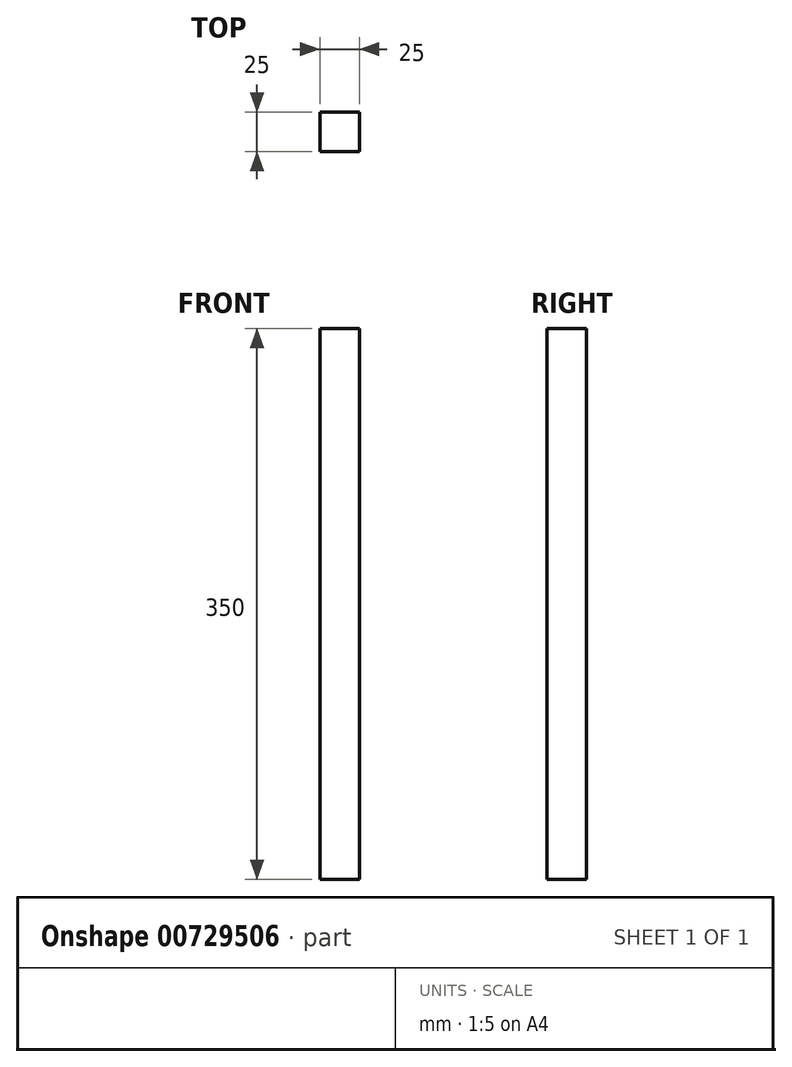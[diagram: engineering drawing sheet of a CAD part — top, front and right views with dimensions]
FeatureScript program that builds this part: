
annotation { "Feature Type Name" : "Feature", "Feature Type Description" : "" }
export const myFeature = defineFeature(function(context is Context, id is Id, definition is map)
    precondition{}
    {
        {
            var Q0;
            Q0=qCreatedBy(makeId("Top.planeOp"),FACE);
            var sketch = newSketch(context, id + "F0", { "sketchPlane" : qUnion([Q0])});
            skLineSegment(sketch, "E0.bottom", {"start": v(-2.89, -1.45) * mm, "end": v(22.11, -1.45) * mm});
            skLineSegment(sketch, "E0.top", {"start": v(-2.89, -26.45) * mm, "end": v(22.11, -26.45) * mm});
            skLineSegment(sketch, "E0.left", {"start": v(-2.89, -1.45) * mm, "end": v(-2.89, -26.45) * mm});
            skLineSegment(sketch, "E0.right", {"start": v(22.11, -1.45) * mm, "end": v(22.11, -26.45) * mm});
            skSolve(sketch);
        }
        {
            var Q0;
            Q0=makeQuery(id+"F0.imprint","IMPRINT",FACE,{"disambiguationData":[TD([[makeQuery(id+"F0.imprint","IMPRINT",EDGE,{"derivedFrom":sQuery(id+"F0.wireOp",EDGE,"E0.bottom")}),-1.0]])]});
            extrude(context, id + "F1", {"entities" : qUnion([Q0]), "oppositeDirection" : true, "depth" : 350 * mm, "offsetDistance" : 25 * mm});
        }
    });
